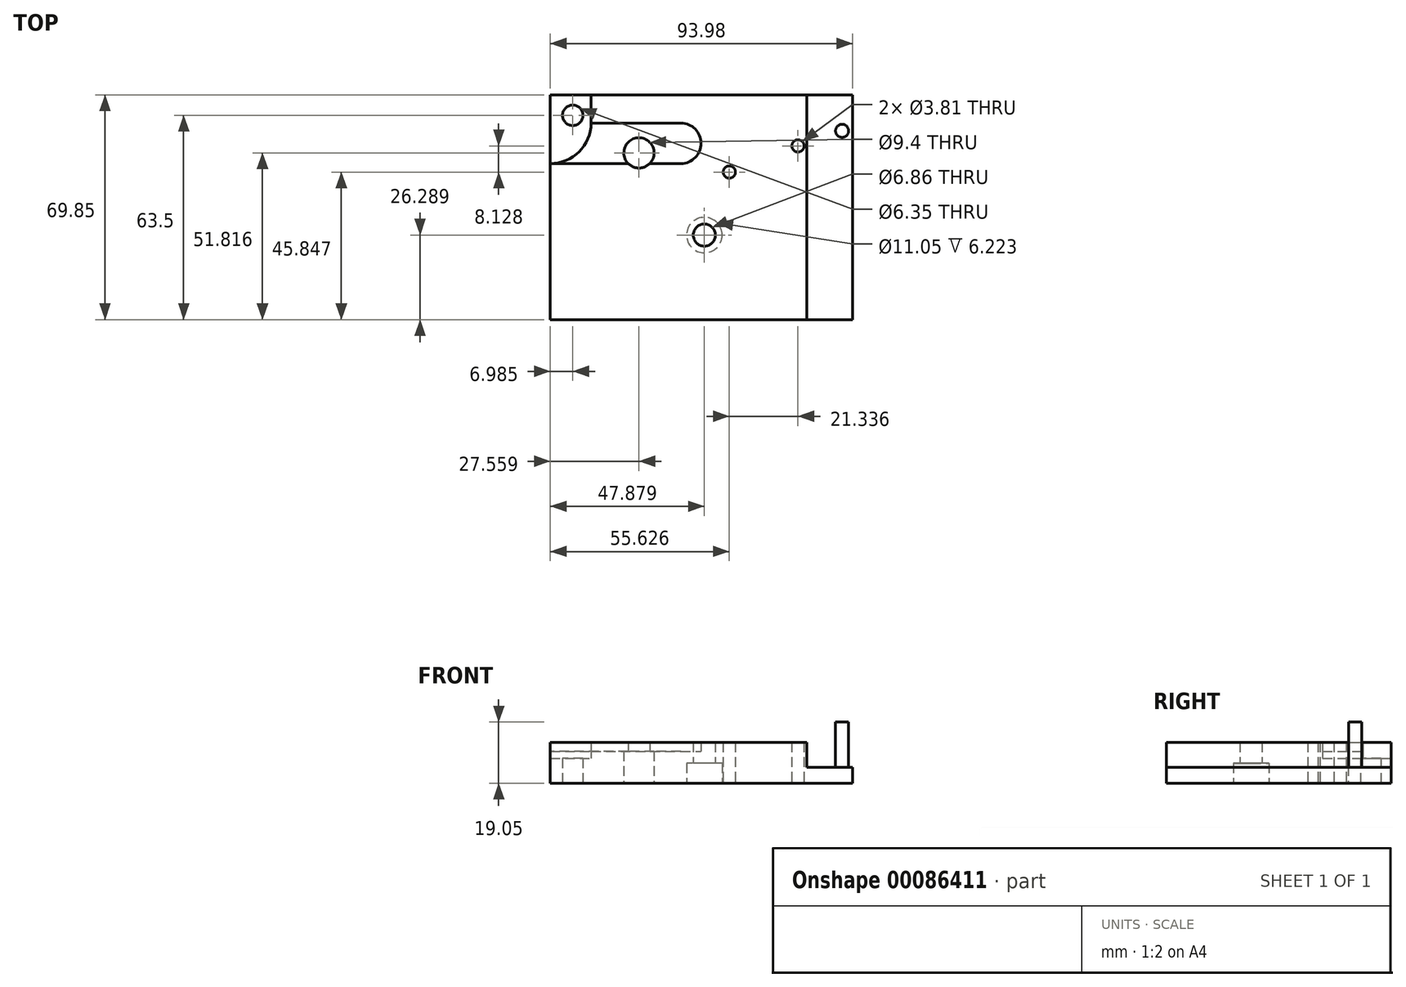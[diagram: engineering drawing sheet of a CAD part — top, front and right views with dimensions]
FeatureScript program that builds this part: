
annotation { "Feature Type Name" : "Feature", "Feature Type Description" : "" }
export const myFeature = defineFeature(function(context is Context, id is Id, definition is map)
    precondition{}
    {
        {
            var Q0;
            Q0=qCreatedBy(makeId("Top.planeOp"),FACE);
            var sketch = newSketch(context, id + "F0", { "sketchPlane" : qUnion([Q0])});
            skLineSegment(sketch, "E0.bottom", {"start": v(0, 0) * mm, "end": v(93.98, 0) * mm});
            skLineSegment(sketch, "E0.top", {"start": v(0, 69.85) * mm, "end": v(93.98, 69.85) * mm});
            skLineSegment(sketch, "E0.left", {"start": v(0, 0) * mm, "end": v(0, 69.85) * mm});
            skLineSegment(sketch, "E0.right", {"start": v(93.98, 0) * mm, "end": v(93.98, 69.85) * mm});
            skLineSegment(sketch, "E1", {"start": v(79.76, 0) * mm, "end": v(79.76, 69.85) * mm});
            skLineSegment(sketch, "E2", {"start": v(0, 48.51) * mm, "end": v(79.76, 48.51) * mm, "construction": true});
            skLineSegment(sketch, "E3", {"start": v(12.7, 48.51) * mm, "end": v(12.7, 69.85) * mm, "construction": true});
            skLineSegment(sketch, "E4", {"start": v(12.7, 61.09) * mm, "end": v(46.86, 61.09) * mm, "construction": true});
            skLineSegment(sketch, "E5", {"start": v(12.7, 54.8) * mm, "end": v(46.86, 54.8) * mm, "construction": true});
            skLineSegment(sketch, "E6", {"start": v(46.86, 61.09) * mm, "end": v(46.86, 48.51) * mm});
            skCircle(sketch, "E7", {"center": v(40.58, 54.8) * mm, "radius": 6.29 * mm, "construction": true});
            skArc(sketch, "E8", {"start": v(46.86, 54.8) * mm, "mid": v(45.02, 59.25) * mm, "end": v(40.58, 61.09) * mm});
            skArc(sketch, "E9", {"start": v(40.58, 48.51) * mm, "mid": v(45.02, 50.36) * mm, "end": v(46.86, 54.8) * mm});
            skLineSegment(sketch, "E10", {"start": v(12.7, 61.09) * mm, "end": v(40.58, 61.09) * mm});
            skLineSegment(sketch, "E11", {"start": v(12.7, 61.09) * mm, "end": v(12.7, 69.85) * mm});
            skLineSegment(sketch, "E12", {"start": v(40.58, 48.51) * mm, "end": v(0, 48.51) * mm});
            skArc(sketch, "E13", {"start": v(0, 48.51) * mm, "mid": v(8.94, 52.19) * mm, "end": v(12.7, 61.09) * mm});
            skCircle(sketch, "E14", {"center": v(6.98, 63.5) * mm, "radius": 3.18 * mm});
            skCircle(sketch, "E15", {"center": v(27.56, 51.82) * mm, "radius": 4.7 * mm});
            skCircle(sketch, "E16", {"center": v(47.88, 26.29) * mm, "radius": 3.43 * mm});
            skCircle(sketch, "E17", {"center": v(76.96, 53.97) * mm, "radius": 1.9 * mm});
            skCircle(sketch, "E18", {"center": v(55.63, 45.85) * mm, "radius": 1.9 * mm});
            skCircle(sketch, "E19", {"center": v(90.68, 58.67) * mm, "radius": 2.03 * mm});
            skSolve(sketch);
        }
        {
            var Q0;
            {var subQ0=sQuery(id+"F0.wireOp",EDGE,"E0.right");Q0=makeQuery(id+"F0.imprint","IMPRINT",FACE,{"disambiguationData":[TD([[makeQuery(id+"F0.imprint","IMPRINT",EDGE,{"derivedFrom":subQ0}),1.0]])]});}
            extrude(context, id + "F1", {"entities" : qUnion([Q0]), "depth" : 4.95 * mm});
        }
        {
            var Q0;
            {var subQ0=sQuery(id+"F0.wireOp",EDGE,"E1");Q0=makeQuery(id+"F0.imprint","IMPRINT",FACE,{"disambiguationData":[TD([[makeQuery(id+"F0.imprint","IMPRINT",EDGE,{"derivedFrom":subQ0}),1.0]])]});}
            extrude(context, id + "F2", {"entities" : qUnion([Q0]), "operationType" : NewBodyOperationType.ADD, "depth" : 12.7 * mm});
        }
        {
            var Q0;
            Q0=makeQuery(id+"F0.imprint","IMPRINT",FACE,{"disambiguationData":[TD([[makeQuery(id+"F0.imprint","IMPRINT",EDGE,{"derivedFrom":sQuery(id+"F0.wireOp",EDGE,"E8")}),1.0]])]});
            extrude(context, id + "F3", {"entities" : qUnion([Q0]), "operationType" : NewBodyOperationType.ADD, "depth" : 9.9 * mm});
        }
        {
            var Q0;
            {var subQ3=sQuery(id+"F0.wireOp",EDGE,"E11");Q0=makeQuery(id+"F0.imprint","IMPRINT",FACE,{"disambiguationData":[TD([[makeQuery(id+"F0.imprint","IMPRINT",EDGE,{"derivedFrom":subQ3}),1.0]])]});}
            extrude(context, id + "F4", {"entities" : qUnion([Q0]), "operationType" : NewBodyOperationType.ADD, "depth" : 7.75 * mm});
        }
        {
            var Q0;
            Q0=makeQuery(id+"F0.imprint","IMPRINT",FACE,{"disambiguationData":[TD([[makeQuery(id+"F0.imprint","IMPRINT",EDGE,{"derivedFrom":sQuery(id+"F0.wireOp",EDGE,"E19")}),1.0]])]});
            extrude(context, id + "F5", {"entities" : qUnion([Q0]), "operationType" : NewBodyOperationType.ADD, "depth" : 19.05 * mm});
        }
        {
            var Q0;
            {var subQ5=sQuery(id+"F0.wireOp",EDGE,"E1");Q0=makeQuery(id+"F0.imprint","IMPRINT",FACE,{"disambiguationData":[TD([[makeQuery(id+"F0.imprint","IMPRINT",EDGE,{"derivedFrom":subQ5}),1.0]])]});}
            var sketch = newSketch(context, id + "F6", { "sketchPlane" : qUnion([Q0])});
            skCircle(sketch, "E20", {"center": v(47.88, 26.29) * mm, "radius": 5.52 * mm});
            skSolve(sketch);
        }
        {
            var Q0;
            Q0=makeQuery(id+"F6.imprint","IMPRINT",FACE,{"disambiguationData":[TD([[makeQuery(id+"F6.imprint","IMPRINT",EDGE,{"derivedFrom":sQuery(id+"F6.wireOp",EDGE,"E20")}),1.0]])]});
            extrude(context, id + "F7", {"entities" : qUnion([Q0]), "operationType" : NewBodyOperationType.REMOVE, "depth" : 6.22 * mm});
        }
    });
